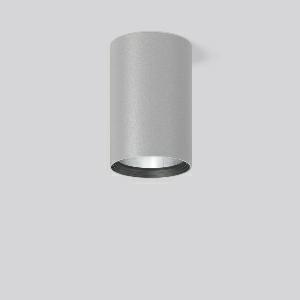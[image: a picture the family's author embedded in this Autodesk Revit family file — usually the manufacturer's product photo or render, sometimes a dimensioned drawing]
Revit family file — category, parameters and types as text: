
# Revit family: heledon_maxi_a_931216_004_3_260b
name_source: partatom
category: Lighting Fixtures
units: mm (PartAtom-declared; Revit-internal decimal feet)

## family parameters
Cut with Voids When Loaded = No
Host = Face
Light Source = No
Part Type = Normal
Room Calculation Point = No
Round Connector Dimension = Use Diameter
Shared = No

## types (1)
- HELEDON maxi A (1 x LED Modul 935, 3300 lm, 3500)
    Apparent Load = 25 VA
    Approval mark = CE
    CIE Flux Codes = 100 100 100 100 100
    Color Rendering = 92
    Color Temperature = 3500
    Default Elevation = 1800 mm
    Description = Series: HELEDON maxi
Cylindrical surface-mounted downlight. Housing: die-cast aluminium, powder-coated. Internal ceiling frame polycarbonate with bayonet mounting. Black plastic ring and recessed LED to prevent glare from the side. Optical assembly with reflector made of MIRO-Silver with 98% total light reflection for outstanding efficiency - can be changed without tools. Best colour rendering index Ra>90. Suitable for Ceiling mounting. Easy installation with a separate ceiling frame with bayonet mounting and plug connection. Driver integrated. Connected via plug-in connector. High quality converter without flickering and stroboscopic effect. The following accessories can be mounted without use of tools: interchangeable lenses, decorative glasses, honeycomb louvre, clear and frosted diffusers, white interchangeable plastic ring. 
Colour: silver
Diameter: 123 mm
Height: 183 mm
Lamp: LED
Socket: without socket
Colour temperature: 3500K
Colour rendering index (CRI): 92
System power: 25 W
Rated luminous flux: 3300 lm
Luminous efficiency: 132 lm/W
Control gear: Regulated power supply
Protection class: I
Type of protection: IP 20
    Height = 183 mm
    Lamp = 1 x LED Modul 935
    Lamp Light Flux = 3300 lm
    Lamp count = 1
    Length = 123 mm
    Lifetime = 50000 h
    Luminous efficacy = 132 lm/W
    Manufacturer = RZB
    ModVariant = No
    Model = 931216.004.3
    Mounting Place = Ceiling
    Mounting Type = Surface mounted
    Number of Poles = 1
    OnlyDefault = Yes
    Power Factor = 1
    Product Name = HELEDON maxi A
    Product group = Surface mounted downlights
    ProductGroupID = 302
    Protection Class = Protection class I
    Protection Degree = IP 20
    RLX_Detail_Level = 1
    RLX_Emergency_Light_Flux = 0 lm
    RLX_Emergency_Type = 0
    RLX_Emergency_Type_DB = No
    RlxData = <blob elided: 99025 chars, md5=c4aca3d1>
    Socket = socket
    Standby Power = 0 W
    System Light Flux = 3300 lm
    System Power = 25 W
    Type Comments = Product without accessories
    Type Image = 931192.004.jpg
    URL = http://relux.com
    VarID = ---
    Voltage = 230 V
    Voltage Range = 220-240 V
    Weight = 0.00 kg
    Width = 0 mm  [stored 0 ft]

note: [stored X ft] marks values corroborated as IEEE doubles in the binary element streams (Revit-internal decimal feet)

## geometry (parser evidence)
native form markers: Blend x4, Sweep x10
no freeform markers — native parametric forms only
